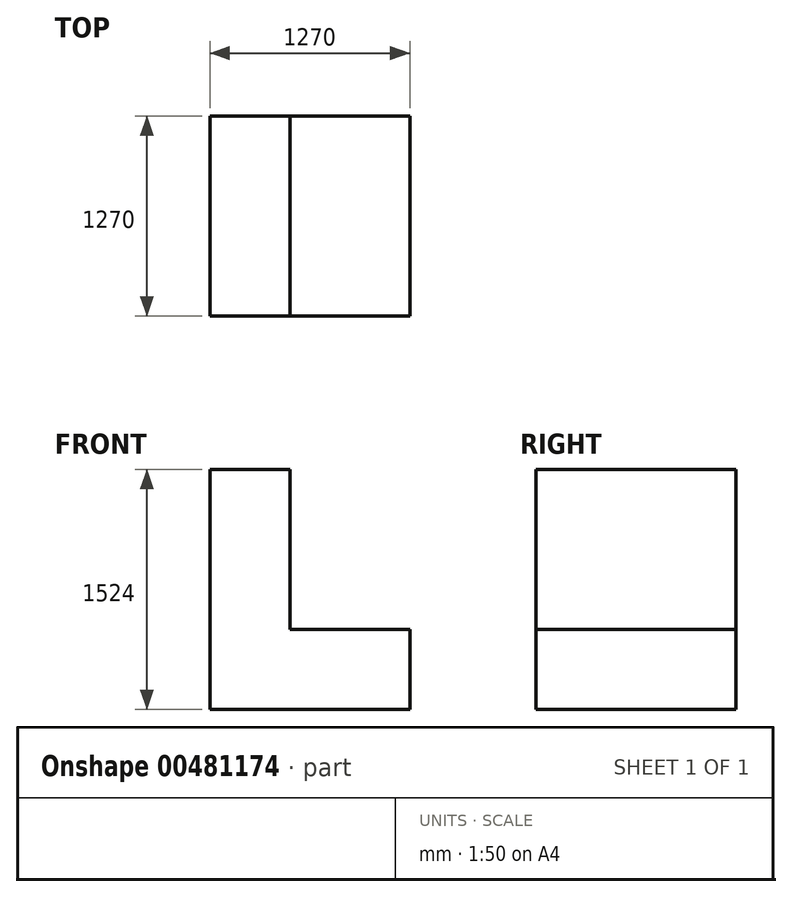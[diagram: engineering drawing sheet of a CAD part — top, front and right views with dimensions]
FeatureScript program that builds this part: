
annotation { "Feature Type Name" : "Feature", "Feature Type Description" : "" }
export const myFeature = defineFeature(function(context is Context, id is Id, definition is map)
    precondition{}
    {
        {
            var Q0;
            Q0=qCreatedBy(makeId("Front.planeOp"),FACE);
            var sketch = newSketch(context, id + "F0", { "sketchPlane" : qUnion([Q0])});
            skLineSegment(sketch, "E0", {"start": v(0, 0) * mm, "end": v(1270, 0) * mm});
            skLineSegment(sketch, "E1", {"start": v(1270, 0) * mm, "end": v(1270, 508) * mm});
            skLineSegment(sketch, "E2", {"start": v(1270, 508) * mm, "end": v(508, 508) * mm});
            skLineSegment(sketch, "E3", {"start": v(508, 508) * mm, "end": v(508, 1524) * mm});
            skLineSegment(sketch, "E4", {"start": v(508, 1524) * mm, "end": v(0, 1524) * mm});
            skLineSegment(sketch, "E5", {"start": v(0, 1524) * mm, "end": v(0, 0) * mm});
            skSolve(sketch);
        }
        {
            var Q0;
            Q0=makeQuery(id+"F0.imprint","IMPRINT",FACE,{"disambiguationData":[TD([[makeQuery(id+"F0.imprint","IMPRINT",EDGE,{"derivedFrom":sQuery(id+"F0.wireOp",EDGE,"E0")}),1.0]])]});
            extrude(context, id + "F1", {"entities" : qUnion([Q0]), "depth" : 1270 * mm});
        }
    });
